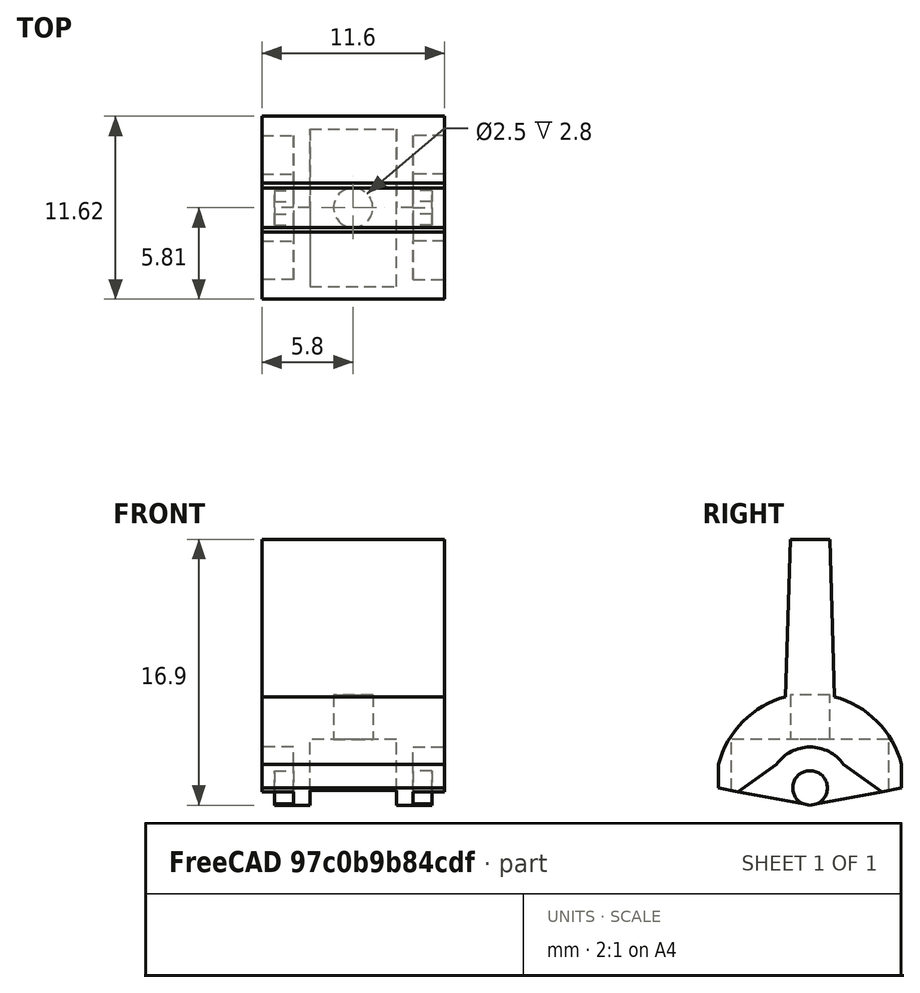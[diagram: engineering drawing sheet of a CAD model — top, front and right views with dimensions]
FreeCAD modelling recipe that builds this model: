
FCSTD DOCUMENT  (FreeCAD 0.21R33771 (Git))
Label: switch lever MA
License: All rights reserved
LicenseURL: http://en.wikipedia.org/wiki/All_rights_reserved
objects: Sketcher::SketchObject×6, PartDesign::Pocket×4, PartDesign::Pad×2, PartDesign::Mirrored×2, PartDesign::Body×1, Mesh::Feature×1
note: 21 computed .brp shape members not serialized (recipe doc carries the construction recipe); baked Part::Feature solids carry a one-line shape summary decoded from their .brp

FEATURE [Sketcher::SketchObject] Sketch
  FullyConstrained = true
  MapMode = 5
  Support = -> [XY_Plane]
  sketch-geometry (8):
    g0: LineSegment StartX=-15.7963 StartY=1.25 StartZ=0 EndX=-15.7963 EndY=-1.25 EndZ=0
    g1: LineSegment StartX=-15.7963 StartY=-1.25 StartZ=0 EndX=-5.79634 EndY=-1.55 EndZ=0
    g2: LineSegment StartX=-15.7963 StartY=1.25 StartZ=0 EndX=-5.79634 EndY=1.55 EndZ=0
    g3: ArcOfCircle CenterX=0 CenterY=0 CenterZ=0 NormalX=0 NormalY=0 NormalZ=1 AngleXU=0 Radius=6 StartAngle=1.82348 EndAngle=2.8803
    g4: ArcOfCircle CenterX=0 CenterY=0 CenterZ=0 NormalX=0 NormalY=0 NormalZ=1 AngleXU=0 Radius=6 StartAngle=3.40289 EndAngle=4.45971
    g5: LineSegment StartX=-1.5 StartY=5.80948 StartZ=0 EndX=1.1 EndY=5.80948 EndZ=0
    g6: LineSegment StartX=1.1 StartY=5.80948 StartZ=0 EndX=1.1 EndY=-5.80948 EndZ=0
    g7: LineSegment StartX=1.1 StartY=-5.80948 StartZ=0 EndX=-1.5 EndY=-5.80948 EndZ=0
  constraints (22):
    c: Coincident(g0,g1)
    c: Coincident(g0,g2)
    c: Coincident(g3,g-1)
    c: Coincident(g3,g2)
    c: Coincident(g4,g3)
    c: Coincident(g4,g1)
    c: Symmetric(g2,g1,g-1)
    c: Symmetric(g0,g0,g-1)
    c: Radius(g3) = 6
    c: Coincident(g5,g6)
    c: Vertical(g6)
    c: Coincident(g6,g7)
    c: Coincident(g7,g4)
    c: Horizontal(g5)
    c: Horizontal(g7)
    c: Coincident(g5,g3)
    c: Vertical(g4,g3)
    c: DistanceX(g3,g-1) = 1.5
    c: DistanceX(g5,g5) = 2.6
    c: DistanceX(g2,g2) = 10
    c: DistanceY(g1,g2) = 3.1
    c: DistanceY(g0,g0) = 2.5
FEATURE [PartDesign::Pad] Pad
  Direction = (0,0,1)
  Length = 11.6
  Length2 = 10
  Midplane = true
  Profile = -> Sketch
  ReferenceAxis = -> Sketch [N_Axis]
  Type = 0
FEATURE [Sketcher::SketchObject] Sketch001
  ExternalGeometry = -> [Pad]
  FullyConstrained = false
  MapMode = 5
  Placement = pos=(0,0,5.8) rot=(0,0,1;0rad)
  Support = -> [Pad]
  sketch-geometry (4):
    g0: ArcOfCircle CenterX=-4e-16 CenterY=-3e-16 CenterZ=0 NormalX=0 NormalY=0 NormalZ=1 AngleXU=0 Radius=2.6 StartAngle=2.18575 EndAngle=4.09743
    g1: LineSegment StartX=1.1 StartY=-5.80948 StartZ=0 EndX=-1.5 EndY=-2.12368 EndZ=0
    g2: LineSegment StartX=1.1 StartY=-5.80948 StartZ=0 EndX=1.1 EndY=5.80948 EndZ=0
    g3: LineSegment StartX=1.1 StartY=5.80948 StartZ=0 EndX=-1.5 EndY=2.12368 EndZ=0
  constraints (9):
    c: DistanceX(g0,g-3) = 2.6
    c: Vertical(g0,g0)
    c: Radius(g0) = 2.6
    c: Coincident(g2,g-4)
    c: Coincident(g3,g0)
    c: Coincident(g1,g0)
    c: Coincident(g1,g2)
    c: Coincident(g1,g-5)
    c: Coincident(g3,g2)
FEATURE [PartDesign::Pocket] Pocket
  BaseFeature = -> Pad
  Direction = (0,0,-1)
  Length = 2
  Length2 = 5
  Profile = -> Sketch001
  ReferenceAxis = -> Sketch001 [N_Axis]
  Type = 0
FEATURE [PartDesign::Mirrored] Mirrored
  BaseFeature = -> Pocket
  MirrorPlane = -> XY_Plane
  Originals = -> [Pocket]
FEATURE [Sketcher::SketchObject] Sketch002
  FullyConstrained = true
  MapMode = 5
  Placement = pos=(0,0,-3.8) rot=(1,0,0;3.14159rad)
  Support = -> [Mirrored]
  sketch-geometry (1):
    g0: Circle CenterX=0 CenterY=0 CenterZ=0 NormalX=0 NormalY=0 NormalZ=1 AngleXU=0 Radius=1.1
  constraints (2):
    c: Coincident(g0,g-1)
    c: Diameter(g0) = 2.2
FEATURE [PartDesign::Pad] Pad001
  BaseFeature = -> Mirrored
  Direction = (0,0,-1)
  Length = 1.2
  Length2 = 10
  Profile = -> Sketch002
  ReferenceAxis = -> Sketch002 [N_Axis]
  Type = 0
FEATURE [PartDesign::Mirrored] Mirrored001
  BaseFeature = -> Pad001
  MirrorPlane = -> XY_Plane
  Originals = -> [Pad001]
FEATURE [Sketcher::SketchObject] Sketch003
  FullyConstrained = true
  MapMode = 5
  Placement = pos=(1.1,0,0) rot=(0.57735,0.57735,0.57735;2.0944rad)
  Support = -> [Mirrored001]
  sketch-geometry (4):
    g0: LineSegment StartX=-5 StartY=2.75 StartZ=0 EndX=5 EndY=2.75 EndZ=0
    g1: LineSegment StartX=5 StartY=2.75 StartZ=0 EndX=5 EndY=-2.75 EndZ=0
    g2: LineSegment StartX=5 StartY=-2.75 StartZ=0 EndX=-5 EndY=-2.75 EndZ=0
    g3: LineSegment StartX=-5 StartY=-2.75 StartZ=0 EndX=-5 EndY=2.75 EndZ=0
  constraints (11):
    c: Coincident(g0,g1)
    c: Coincident(g1,g2)
    c: Coincident(g2,g3)
    c: Coincident(g3,g0)
    c: Horizontal(g0)
    c: Horizontal(g2)
    c: Vertical(g1)
    c: Vertical(g3)
    c: Symmetric(g0,g1,g-1)
    c: DistanceX(g0,g0) = 10
    c: DistanceY(g3,g3) = 5.5
FEATURE [PartDesign::Pocket] Pocket001
  BaseFeature = -> Mirrored001
  Direction = (-1,0,0)
  Length = 4.2
  Length2 = 5
  Profile = -> Sketch003
  ReferenceAxis = -> Sketch003 [N_Axis]
  Type = 0
FEATURE [Sketcher::SketchObject] Sketch004
  FullyConstrained = true
  MapMode = 5
  Placement = pos=(-3.1,0,0) rot=(0.57735,0.57735,0.57735;2.0944rad)
  Support = -> [Pocket001]
  sketch-geometry (1):
    g0: Circle CenterX=0 CenterY=0 CenterZ=0 NormalX=0 NormalY=0 NormalZ=1 AngleXU=0 Radius=1.25
  constraints (2):
    c: Coincident(g0,g-1)
    c: Diameter(g0) = 2.5
FEATURE [PartDesign::Pocket] Pocket002
  BaseFeature = -> Pocket001
  Direction = (-1,0,0)
  Length = 2.8
  Length2 = 5
  Profile = -> Sketch004
  ReferenceAxis = -> Sketch004 [N_Axis]
  Type = 0
FEATURE [Sketcher::SketchObject] Sketch005
  ExternalGeometry = -> [Pocket002]
  FullyConstrained = false
  MapMode = 5
  Placement = pos=(0,0,5.8) rot=(0,0,1;0rad)
  Support = -> [Pocket002]
  sketch-geometry (5):
    g0: LineSegment StartX=1.1 StartY=0 StartZ=0 EndX=0 EndY=-5.80948 EndZ=0
    g1: LineSegment StartX=1.1 StartY=0 StartZ=0 EndX=0 EndY=5.80948 EndZ=0
    g2: LineSegment StartX=0 StartY=5.80948 StartZ=0 EndX=1.32725 EndY=5.80948 EndZ=0
    g3: LineSegment StartX=1.32725 StartY=5.80948 StartZ=0 EndX=1.32725 EndY=-5.80948 EndZ=0
    g4: LineSegment StartX=0 StartY=-5.80948 StartZ=0 EndX=1.32725 EndY=-5.80948 EndZ=0
  constraints (14):
    c: PointOnObject(g0,g-1)
    c: PointOnObject(g0,g-4)
    c: Coincident(g1,g0)
    c: PointOnObject(g1,g-3)
    c: Coincident(g2,g1)
    c: Horizontal(g2)
    c: Coincident(g3,g2)
    c: Vertical(g3)
    c: Coincident(g4,g0)
    c: Coincident(g4,g3)
    c: PointOnObject(g-4,g4)
    c: PointOnObject(g0,g-2)
    c: PointOnObject(g1,g-2)
    c: PointOnObject(g0,g-5)
FEATURE [PartDesign::Pocket] Pocket003
  BaseFeature = -> Pocket002
  Direction = (0,0,-1)
  Length = 5
  Length2 = 5
  Profile = -> Sketch005
  ReferenceAxis = -> Sketch005 [N_Axis]
  Type = 1
FEATURE [PartDesign::Body] Body
  Group = -> [Sketch,Pad,Sketch001,Pocket,Mirrored,Sketch002,Pad001,Mirrored001,Sketch003,Pocket001,Sketch004,Pocket002,Sketch005,Pocket003]
  Origin = -> Origin
  Placement = pos=(0,0,0) rot=(0,1,0;1.5708rad)
  Tip = -> Pocket003
FEATURE [Mesh::Feature] Mesh  label="Body (Meshed)"
